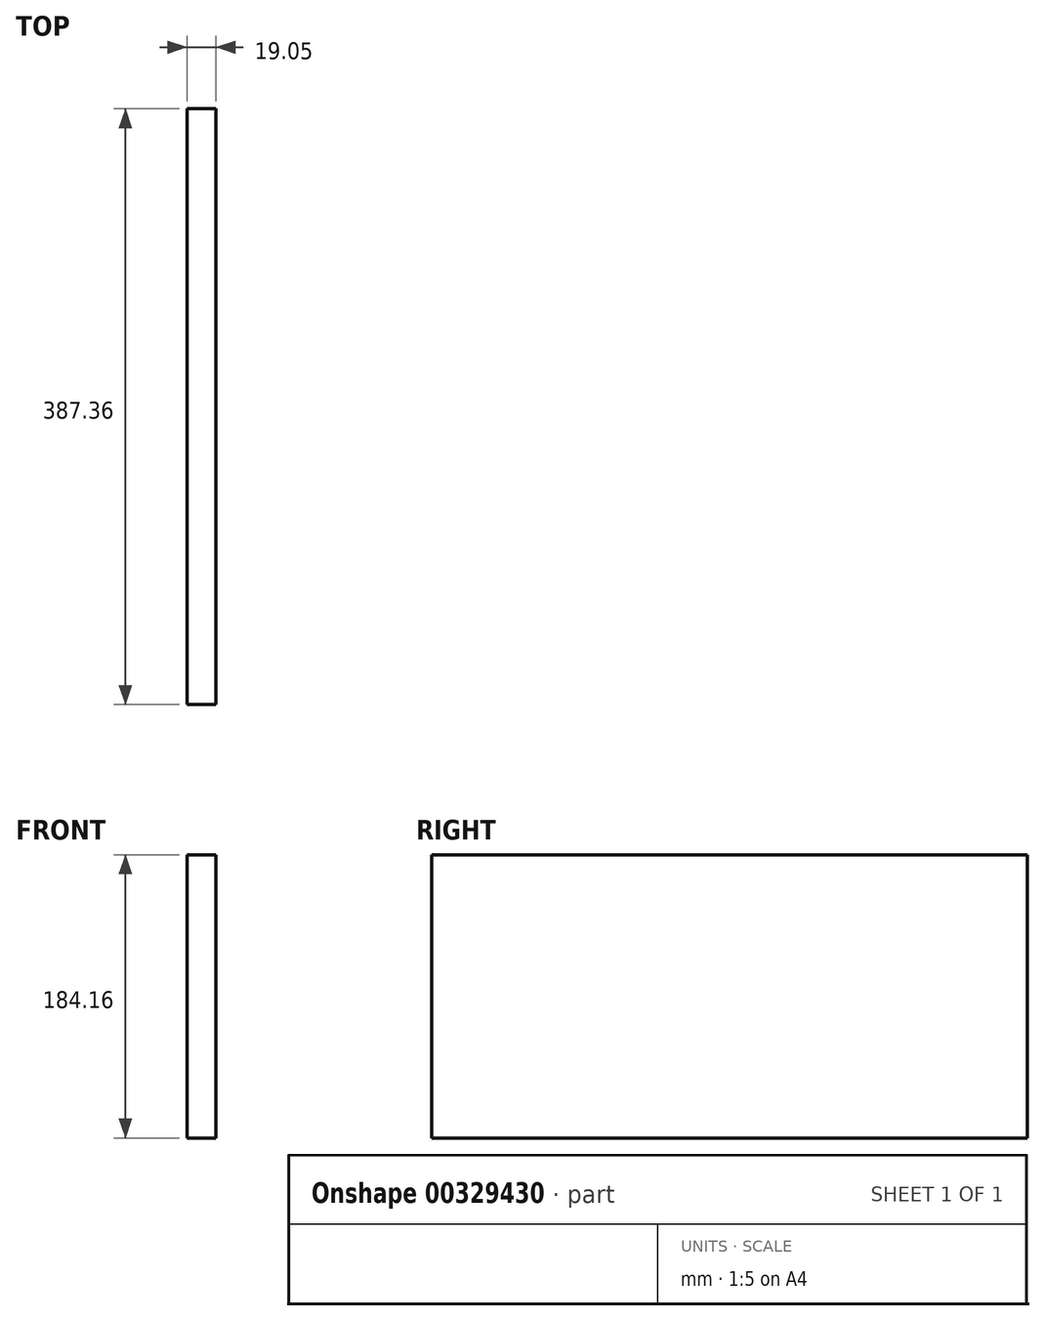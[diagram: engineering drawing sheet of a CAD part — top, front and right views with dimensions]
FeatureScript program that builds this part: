
annotation { "Feature Type Name" : "Feature", "Feature Type Description" : "" }
export const myFeature = defineFeature(function(context is Context, id is Id, definition is map)
    precondition{}
    {
        {
            var Q0;
            Q0=qCreatedBy(makeId("Right.planeOp"),FACE);
            var sketch = newSketch(context, id + "F0", { "sketchPlane" : qUnion([Q0])});
            skLineSegment(sketch, "E0.bottom", {"start": v(-193.68, 92.08) * mm, "end": v(193.68, 92.08) * mm});
            skLineSegment(sketch, "E0.top", {"start": v(-193.68, -92.08) * mm, "end": v(193.68, -92.08) * mm});
            skLineSegment(sketch, "E0.left", {"start": v(-193.68, 92.08) * mm, "end": v(-193.68, -92.08) * mm});
            skLineSegment(sketch, "E0.right", {"start": v(193.68, 92.08) * mm, "end": v(193.68, -92.08) * mm});
            skPoint(sketch, "E0.middle", {"position": v(0, 0) * mm});
            skSolve(sketch);
        }
        {
            var Q0;
            Q0=qSketchRegion(id+"F0",true);
            extrude(context, id + "F1", {"entities" : qUnion([Q0]), "depth" : 19.05 * mm});
        }
    });
